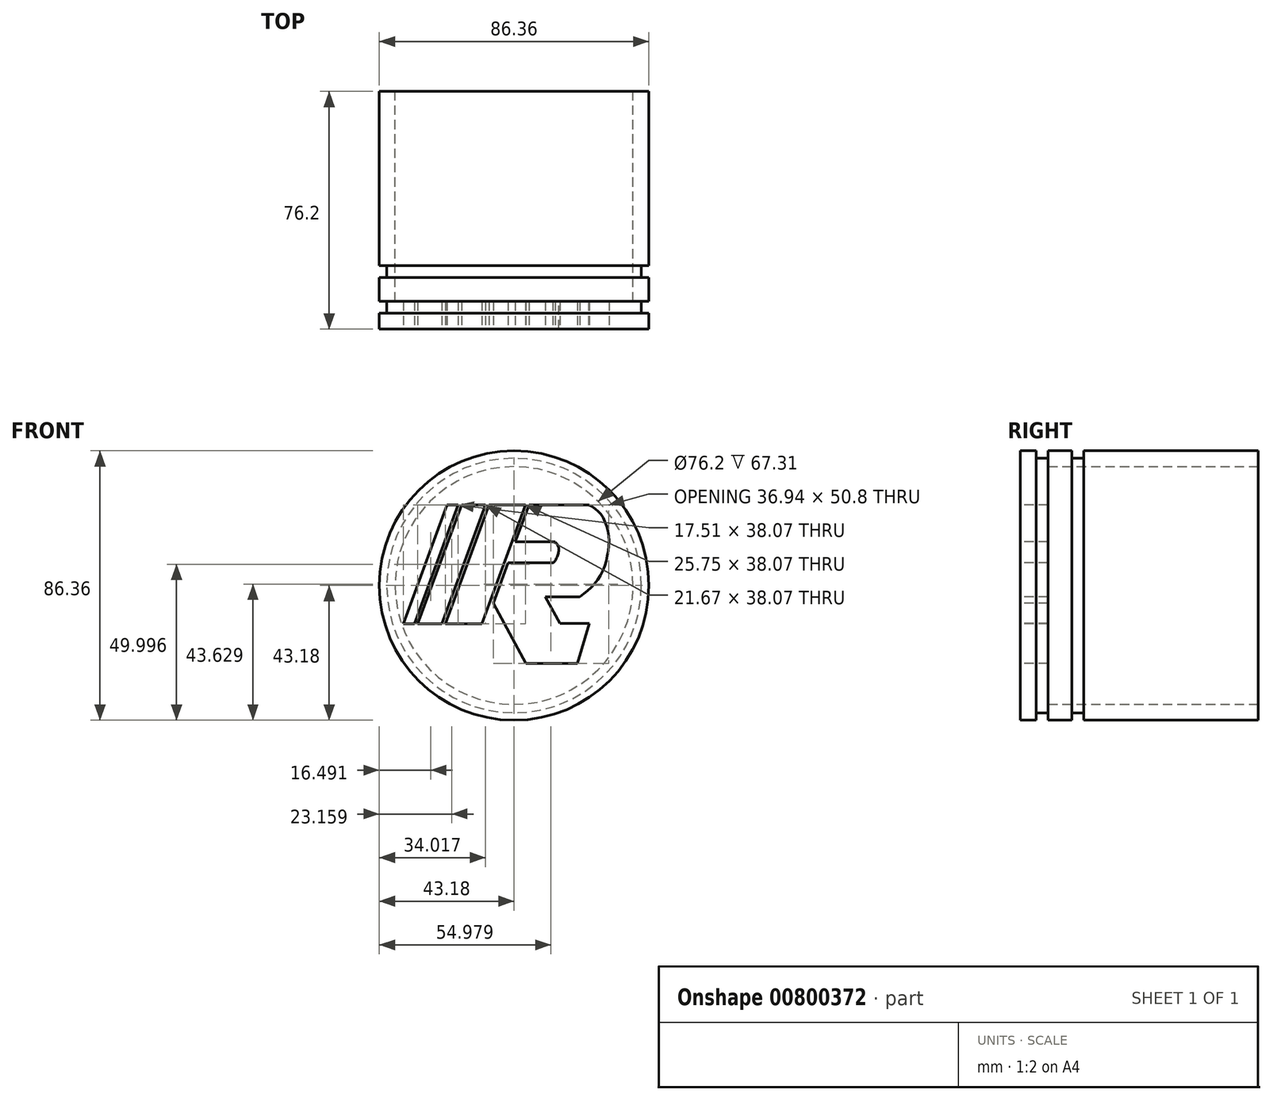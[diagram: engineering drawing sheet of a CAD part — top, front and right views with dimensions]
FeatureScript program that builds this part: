
annotation { "Feature Type Name" : "Feature", "Feature Type Description" : "" }
export const myFeature = defineFeature(function(context is Context, id is Id, definition is map)
    precondition{}
    {
        {
            var Q0;
            Q0=qCreatedBy(makeId("Front.planeOp"),FACE);
            var sketch = newSketch(context, id + "F0", { "sketchPlane" : qUnion([Q0])});
            skCircle(sketch, "E0", {"center": v(0, 0) * mm, "radius": 43.18 * mm});
            skSolve(sketch);
        }
        {
            var Q0;
            Q0 = qSketchRegion(id + "F0", true);
            extrude(context, id + "F1", {"entities" : qUnion([Q0]), "oppositeDirection" : true, "depth" : 76.2 * mm, "offsetDistance" : 25.4 * mm});
        }
        {
            var Q0;
            Q0=qCreatedBy(makeId("Front.planeOp"),FACE);
            var sketch = newSketch(context, id + "F2", { "sketchPlane" : qUnion([Q0])});
            skLineSegment(sketch, "E1", {"start": v(-35.44, -12.22) * mm, "end": v(-21.43, 25.85) * mm});
            skLineSegment(sketch, "E2", {"start": v(-10.3, -12.22) * mm, "end": v(-22.04, -12.22) * mm});
            skLineSegment(sketch, "E3", {"start": v(-17.94, 25.85) * mm, "end": v(-31.94, -12.22) * mm});
            skLineSegment(sketch, "E4", {"start": v(-30.86, -12.22) * mm, "end": v(-16.85, 25.85) * mm});
            skLineSegment(sketch, "E5", {"start": v(-9.19, 25.85) * mm, "end": v(-23.2, -12.22) * mm});
            skLineSegment(sketch, "E6", {"start": v(-22.04, -12.22) * mm, "end": v(-8.03, 25.85) * mm});
            skLineSegment(sketch, "E7", {"start": v(3.71, 25.85) * mm, "end": v(-10.3, -12.22) * mm});
            skLineSegment(sketch, "E8", {"start": v(0.4, 13.97) * mm, "end": v(4.78, 25.85) * mm});
            skLineSegment(sketch, "E9", {"start": v(0.4, 13.97) * mm, "end": v(13.14, 13.97) * mm});
            skLineSegment(sketch, "E10", {"start": v(12.45, 7.3) * mm, "end": v(-1.9, 7.3) * mm});
            skLineSegment(sketch, "E11", {"start": v(-1.9, 7.3) * mm, "end": v(-6.67, -5.65) * mm});
            skLineSegment(sketch, "E12", {"start": v(-6.67, -5.65) * mm, "end": v(3.84, -24.95) * mm});
            skLineSegment(sketch, "E13", {"start": v(3.84, -24.95) * mm, "end": v(20.27, -24.95) * mm});
            skLineSegment(sketch, "E14", {"start": v(20.27, -24.95) * mm, "end": v(24.16, -12.13) * mm});
            skLineSegment(sketch, "E15", {"start": v(24.16, -12.13) * mm, "end": v(14.67, -12.13) * mm});
            skLineSegment(sketch, "E16", {"start": v(14.67, -12.13) * mm, "end": v(10.02, -3.57) * mm});
            skLineSegment(sketch, "E17", {"start": v(10.02, -3.57) * mm, "end": v(21, -3.57) * mm});
            skFitSpline(sketch, "E18", {"points": [v(23.8, 25.85) * mm, v(26.68, 24.1) * mm, v(28.83, 21.09) * mm, v(30.34, 16) * mm, v(30.05, 10.54) * mm, v(28.4, 4.66) * mm, v(25.17, -0.15) * mm, v(21, -3.57) * mm], "startDerivative": vector(25.95, -13.02) * mm, "endDerivative": vector(-29.28, -21.25) * mm});
            skLineSegment(sketch, "E19.trimOffspring", {"start": v(-17.94, 25.85) * mm, "end": v(-21.43, 25.85) * mm});
            skLineSegment(sketch, "E20.trimOffspring", {"start": v(-9.19, 25.85) * mm, "end": v(-16.85, 25.85) * mm});
            skLineSegment(sketch, "E21.trimOffspring", {"start": v(3.71, 25.85) * mm, "end": v(-8.03, 25.85) * mm});
            skLineSegment(sketch, "E22.trimOffspring", {"start": v(23.8, 25.85) * mm, "end": v(4.78, 25.85) * mm});
            skLineSegment(sketch, "E23.trimOffspring", {"start": v(-23.2, -12.22) * mm, "end": v(-30.86, -12.22) * mm});
            skLineSegment(sketch, "E24.trimOffspring", {"start": v(-31.94, -12.22) * mm, "end": v(-35.44, -12.22) * mm});
            skFitSpline(sketch, "E25", {"points": [v(13.14, 13.97) * mm, v(14.18, 12.43) * mm, v(14.12, 10.25) * mm, v(13.14, 7.96) * mm, v(12.45, 7.3) * mm], "startDerivative": vector(5.02, -5.67) * mm, "endDerivative": vector(-3.78, -2.78) * mm});
            skSolve(sketch);
        }
        {
            var Q0;
            Q0 = qSketchRegion(id + "F2", true);
            extrude(context, id + "F3", {"entities" : qUnion([Q0]), "operationType" : NewBodyOperationType.REMOVE, "endBound" : BoundingType.THROUGH_ALL, "oppositeDirection" : true, "depth" : 6.35 * mm, "offsetDistance" : 25.4 * mm});
        }
        {
            var Q0;
            Q0=makeQuery(id+"F1.opExtrude","CAP_FACE",FACE,{"disambiguationData":[OSD([sQuery(id+"F0.wireOp",EDGE,"E0")])],"isStart":false});
            var sketch = newSketch(context, id + "F4", { "sketchPlane" : qUnion([Q0])});
            skCircle(sketch, "E26", {"center": v(0, 0) * mm, "radius": 38.1 * mm});
            skSolve(sketch);
        }
        {
            var Q0;
            Q0 = qSketchRegion(id + "F4", true);
            extrude(context, id + "F5", {"entities" : qUnion([Q0]), "operationType" : NewBodyOperationType.REMOVE, "oppositeDirection" : true, "depth" : 67.3 * mm, "offsetDistance" : 25.4 * mm});
        }
        {
            var Q0;
            Q0=qCreatedBy(makeId("Right.planeOp"),FACE);
            var sketch = newSketch(context, id + "F6", { "sketchPlane" : qUnion([Q0])});
            skLineSegment(sketch, "E27.bottom", {"start": v(8.9, 43.33) * mm, "end": v(5.08, 43.33) * mm});
            skLineSegment(sketch, "E27.top", {"start": v(8.9, 40.79) * mm, "end": v(5.08, 40.79) * mm});
            skLineSegment(sketch, "E27.left", {"start": v(8.9, 43.33) * mm, "end": v(8.9, 40.79) * mm});
            skLineSegment(sketch, "E27.right", {"start": v(5.08, 43.33) * mm, "end": v(5.08, 40.79) * mm});
            skLineSegment(sketch, "E28.bottom", {"start": v(20.32, 43.33) * mm, "end": v(16.51, 43.33) * mm});
            skLineSegment(sketch, "E28.top", {"start": v(20.32, 40.79) * mm, "end": v(16.51, 40.79) * mm});
            skLineSegment(sketch, "E28.left", {"start": v(20.32, 43.33) * mm, "end": v(20.32, 40.79) * mm});
            skLineSegment(sketch, "E28.right", {"start": v(16.51, 43.33) * mm, "end": v(16.51, 40.79) * mm});
            skLineSegment(sketch, "E29", {"start": v(80.01, 0) * mm, "end": v(-10.15, 0) * mm});
            skSolve(sketch);
        }
        {
            var Q0;
            Q0 = qSketchRegion(id + "F6", true);
            var Q1;
            Q1=sQuery(id+"F6.wireOp",EDGE,"E29");
            revolve(context, id + "F7", {"operationType" : NewBodyOperationType.REMOVE, "surfaceOperationType" : NewSurfaceOperationType.NEW, "entities" : qUnion([Q0]), "axis" : qUnion([Q1]), "revolveType" : RevolveType.FULL, "oppositeDirection" : true});
        }
    });
